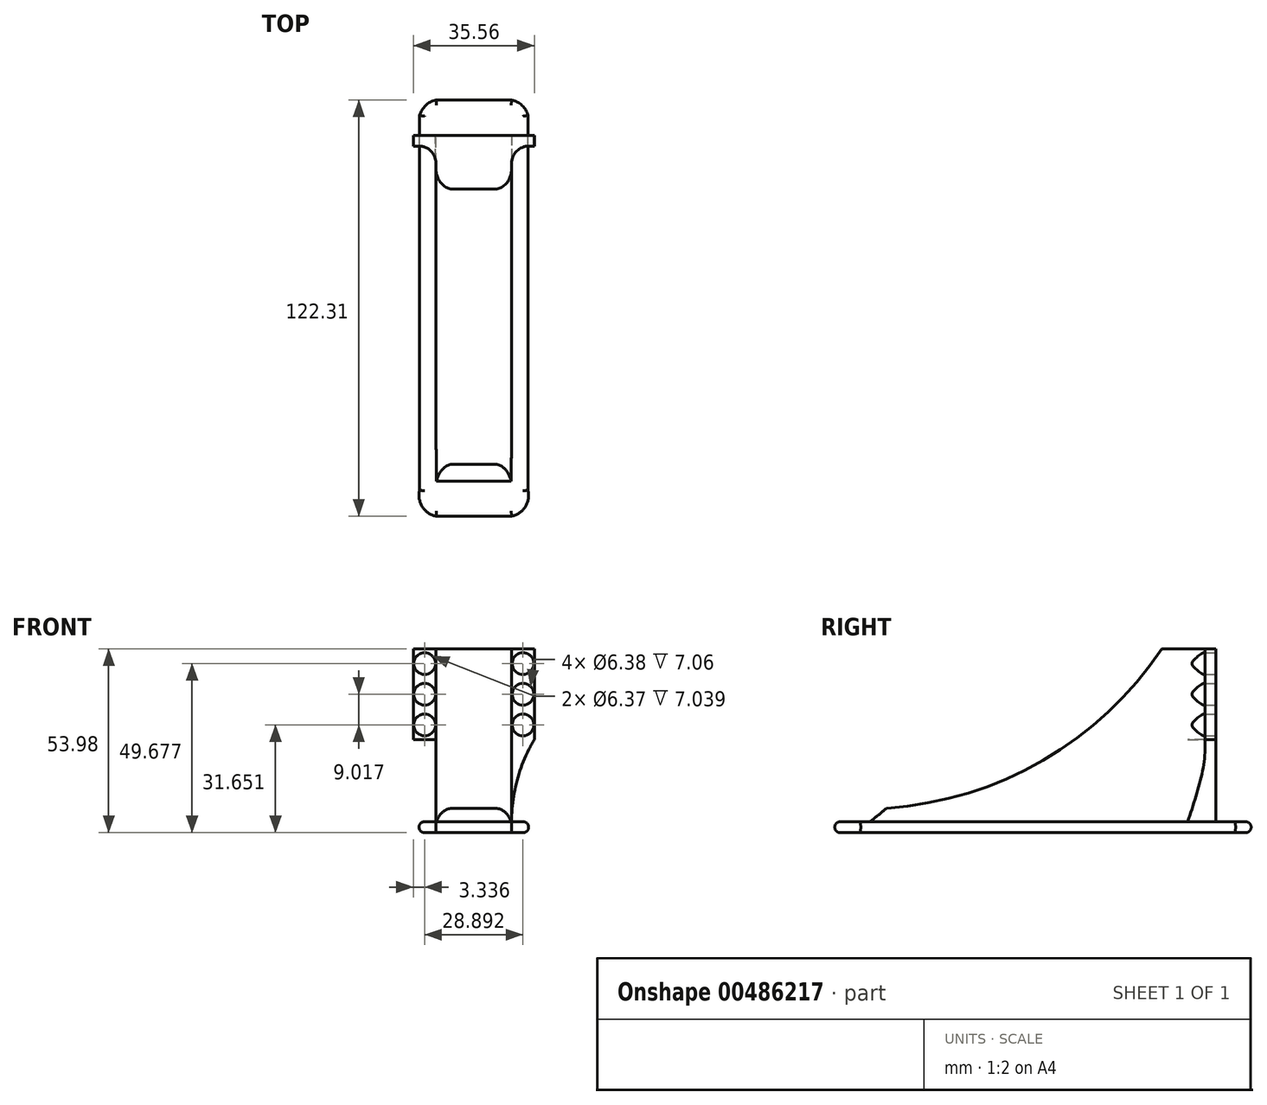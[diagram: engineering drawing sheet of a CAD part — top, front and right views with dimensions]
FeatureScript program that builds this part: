
annotation { "Feature Type Name" : "Feature", "Feature Type Description" : "" }
export const myFeature = defineFeature(function(context is Context, id is Id, definition is map)
    precondition{}
    {
        {
            var Q0;
            Q0=qCreatedBy(makeId("Right.planeOp"),FACE);
            var sketch = newSketch(context, id + "F0", { "sketchPlane" : qUnion([Q0])});
            skLineSegment(sketch, "E0", {"start": v(21.87, 0) * mm, "end": v(21.87, 50.8) * mm});
            skLineSegment(sketch, "E1", {"start": v(21.87, 0) * mm, "end": v(-54.33, 0) * mm});
            skLineSegment(sketch, "E2", {"start": v(21.87, 0) * mm, "end": v(-79.73, 0) * mm});
            skLineSegment(sketch, "E3", {"start": v(-79.73, 0) * mm, "end": v(-79.73, -3.18) * mm});
            skLineSegment(sketch, "E4", {"start": v(-79.73, -3.18) * mm, "end": v(21.87, -3.18) * mm});
            skLineSegment(sketch, "E5", {"start": v(21.87, -3.18) * mm, "end": v(21.87, 0) * mm});
            skLineSegment(sketch, "E6", {"start": v(-79.73, 0) * mm, "end": v(-74.8, 4.01) * mm});
            skLineSegment(sketch, "E7", {"start": v(21.87, 50.8) * mm, "end": v(6.02, 50.8) * mm});
            skArc(sketch, "E8", {"start": v(-74.8, 4.01) * mm, "mid": v(-28.96, 18.01) * mm, "end": v(6.02, 50.8) * mm});
            skSolve(sketch);
        }
        {
            var Q0;
            Q0=makeQuery(id+"F0.imprint","IMPRINT",FACE,{"disambiguationData":[TD([[makeQuery(id+"F0.imprint","IMPRINT",EDGE,{"derivedFrom":sQuery(id+"F0.wireOp",EDGE,"E0")}),1.0]])]});
            extrude(context, id + "F1", {"entities" : qUnion([Q0]), "depth" : 22.22 * mm, "offsetDistance" : 25.4 * mm});
        }
        {
            var Q0;
            Q0=makeQuery(id+"F1.opExtrude","SWEPT_FACE",FACE,{"disambiguationData":[OSD([sQuery(id+"F0.wireOp",EDGE,"E1"),sQuery(id+"F0.wireOp",EDGE,"E2")])]});
            var sketch = newSketch(context, id + "F2", { "sketchPlane" : qUnion([Q0])});
            skLineSegment(sketch, "E9.bottom", {"start": v(27.02, 90.08) * mm, "end": v(-4.8, 90.08) * mm});
            skLineSegment(sketch, "E9.top", {"start": v(27.02, -32.23) * mm, "end": v(-4.8, -32.23) * mm});
            skLineSegment(sketch, "E9.left", {"start": v(27.02, 90.08) * mm, "end": v(27.02, -32.23) * mm});
            skLineSegment(sketch, "E9.right", {"start": v(-4.8, 90.08) * mm, "end": v(-4.8, -32.23) * mm});
            skPoint(sketch, "E9.middle", {"position": v(11.11, 28.93) * mm});
            skPoint(sketch, "E9.middle.positionSnap0", {"position": v(22.23, 28.93) * mm});
            skPoint(sketch, "E9.middle.positionSnap1", {"position": v(11.11, 79.73) * mm});
            skPoint(sketch, "E9.centerSnap0", {"position": v(22.23, 28.93) * mm});
            skPoint(sketch, "E9.centerSnap1", {"position": v(11.11, 79.73) * mm});
            skArc(sketch, "E10", {"start": v(0, 90.08) * mm, "mid": v(-4.03, 87.29) * mm, "end": v(-4.8, 82.44) * mm});
            skLineSegment(sketch, "E11", {"start": v(11.11, 79.73) * mm, "end": v(11.11, -21.87) * mm, "construction": true});
            skLineSegment(sketch, "E12", {"start": v(11.11, 28.93) * mm, "end": v(27.02, 28.93) * mm, "construction": true});
            skArc(sketch, "E13.MirrorCS", {"start": v(22.23, 90.08) * mm, "mid": v(26.26, 87.29) * mm, "end": v(27.02, 82.44) * mm});
            skArc(sketch, "E14.MirrorCS", {"start": v(22.23, -32.23) * mm, "mid": v(26.26, -29.44) * mm, "end": v(27.02, -24.59) * mm});
            skArc(sketch, "E15.MirrorCS", {"start": v(0, -32.23) * mm, "mid": v(-4.03, -29.44) * mm, "end": v(-4.8, -24.59) * mm});
            skSolve(sketch);
        }
        {
            var Q0;
            {var subQ0=sQuery(id+"F2.wireOp",EDGE,"E13.MirrorCS");var subQ1=sQuery(id+"F2.wireOp",EDGE,"E9.left");var subQ2=makeQuery(id+"F2.imprint","INTERSECT",VERTEX,{"disambiguationData":[OD(0.0)],"derivedFrom":[subQ1,subQ0]});Q0=makeQuery(id+"F2.imprint","IMPRINT",FACE,{"disambiguationData":[TD([[makeQuery(id+"F2.imprint","IMPRINT",EDGE,{"disambiguationData":[TD([[subQ2,1.0]])],"derivedFrom":subQ1}),1.0]])]});}
            var Q1;
            {var subQ0=sQuery(id+"F2.wireOp",EDGE,"E14.MirrorCS");var subQ1=sQuery(id+"F2.wireOp",EDGE,"E9.left");var subQ2=makeQuery(id+"F2.imprint","INTERSECT",VERTEX,{"disambiguationData":[OD(0.0)],"derivedFrom":[subQ1,subQ0]});Q1=makeQuery(id+"F2.imprint","IMPRINT",FACE,{"disambiguationData":[TD([[makeQuery(id+"F2.imprint","IMPRINT",EDGE,{"disambiguationData":[TD([[subQ2,-1.0]])],"derivedFrom":subQ1}),1.0]])]});}
            var Q2;
            {var subQ0=sQuery(id+"F2.wireOp",EDGE,"E10");var subQ1=sQuery(id+"F2.wireOp",EDGE,"E9.right");var subQ2=makeQuery(id+"F2.imprint","INTERSECT",VERTEX,{"disambiguationData":[OD(0.0)],"derivedFrom":[subQ1,subQ0]});Q2=makeQuery(id+"F2.imprint","IMPRINT",FACE,{"disambiguationData":[TD([[makeQuery(id+"F2.imprint","IMPRINT",EDGE,{"disambiguationData":[TD([[subQ2,1.0]])],"derivedFrom":subQ1}),-1.0]])]});}
            var Q3;
            {var subQ0=sQuery(id+"F2.wireOp",EDGE,"E15.MirrorCS");var subQ1=sQuery(id+"F2.wireOp",EDGE,"E9.right");var subQ2=makeQuery(id+"F2.imprint","INTERSECT",VERTEX,{"disambiguationData":[OD(0.0)],"derivedFrom":[subQ1,subQ0]});Q3=makeQuery(id+"F2.imprint","IMPRINT",FACE,{"disambiguationData":[TD([[makeQuery(id+"F2.imprint","IMPRINT",EDGE,{"disambiguationData":[TD([[subQ2,-1.0]])],"derivedFrom":subQ1}),-1.0]])]});}
            var Q4;
            {var subQ0=sQuery(id+"F0.wireOp",EDGE,"E1");var subQ1=sQuery(id+"F0.wireOp",EDGE,"E2");Q4=makeQuery(id+"F2.imprint","IMPRINT",FACE,{"disambiguationData":[TD([[makeQuery(id+"F2.imprint","IMPRINT",EDGE,{"derivedFrom":makeQuery(id+"F1.opExtrude","CAP_EDGE",EDGE,{"disambiguationData":[OSD([subQ0,subQ1])],"isStart":true})}),-1.0]])]});}
            var Q5;
            {var subQ15=sQuery(id+"F0.wireOp",EDGE,"E1");var subQ19=sQuery(id+"F0.wireOp",EDGE,"E2");Q5=makeQuery(id+"F2.imprint","IMPRINT",FACE,{"disambiguationData":[TD([[makeQuery(id+"F2.imprint","IMPRINT",EDGE,{"derivedFrom":makeQuery(id+"F1.opExtrude","CAP_EDGE",EDGE,{"disambiguationData":[OSD([subQ15,subQ19])],"isStart":true})}),1.0]])]});}
            extrude(context, id + "F3", {"entities" : qUnion([Q0, Q1, Q2, Q3, Q4, Q5]), "operationType" : NewBodyOperationType.ADD, "depth" : 3.17 * mm, "offsetDistance" : 25.4 * mm});
        }
        {
            var Q0;
            Q0=makeQuery(id+"F1.opExtrude","SWEPT_FACE",FACE,{"disambiguationData":[OSD([sQuery(id+"F0.wireOp",EDGE,"E0")])]});
            var sketch = newSketch(context, id + "F4", { "sketchPlane" : qUnion([Q0])});
            skLineSegment(sketch, "E16.bottom", {"start": v(-11.11, 50.8) * mm, "end": v(6.67, 50.8) * mm});
            skLineSegment(sketch, "E16.top", {"start": v(-11.11, 24.18) * mm, "end": v(6.67, 24.18) * mm});
            skLineSegment(sketch, "E16.left", {"start": v(-11.11, 50.8) * mm, "end": v(-11.11, 24.18) * mm});
            skLineSegment(sketch, "E16.right", {"start": v(6.67, 50.8) * mm, "end": v(6.67, 24.18) * mm});
            skLineSegment(sketch, "E17", {"start": v(0, 50.8) * mm, "end": v(6.67, 50.8) * mm, "construction": true});
            skLineSegment(sketch, "E18", {"start": v(3.33, 50.8) * mm, "end": v(3.33, 24.18) * mm, "construction": true});
            skCircle(sketch, "E19", {"center": v(3.33, 46.5) * mm, "radius": 3.18 * mm});
            skLineSegment(sketch, "E20", {"start": v(3.33, 43.31) * mm, "end": v(3.33, 39.35) * mm, "construction": true});
            skCircle(sketch, "E21", {"center": v(3.33, 37.49) * mm, "radius": 3.19 * mm});
            skLineSegment(sketch, "E22", {"start": v(3.33, 46.5) * mm, "end": v(3.33, 37.49) * mm});
            skLineSegment(sketch, "E23", {"start": v(3.33, 37.49) * mm, "end": v(3.33, 28.47) * mm});
            skCircle(sketch, "E24", {"center": v(3.33, 28.47) * mm, "radius": 3.19 * mm});
            skLineSegment(sketch, "E25.MirrorCS", {"start": v(-11.11, 50.8) * mm, "end": v(-28.9, 50.8) * mm});
            skLineSegment(sketch, "E26.MirrorCS", {"start": v(-11.11, 24.18) * mm, "end": v(-28.9, 24.18) * mm});
            skLineSegment(sketch, "E27.MirrorCS", {"start": v(-28.9, 50.8) * mm, "end": v(-28.9, 24.18) * mm});
            skCircle(sketch, "E28.MirrorC", {"center": v(-25.56, 37.49) * mm, "radius": 3.19 * mm});
            skCircle(sketch, "E29.MirrorC", {"center": v(-25.56, 28.47) * mm, "radius": 3.19 * mm});
            skCircle(sketch, "E30.MirrorC", {"center": v(-25.56, 46.5) * mm, "radius": 3.18 * mm});
            skArc(sketch, "E31", {"start": v(-22.22, 0) * mm, "mid": v(-23.92, 12.54) * mm, "end": v(-28.9, 24.18) * mm});
            skArc(sketch, "E32.MirrorCS", {"start": v(0, 0) * mm, "mid": v(1.7, 12.54) * mm, "end": v(6.67, 24.18) * mm});
            skSolve(sketch);
        }
        {
            var Q0;
            Q0 = qSketchRegion(id + "F4", true);
            var Q1;
            {var subQ0=sQuery(id+"F4.wireOp",EDGE,"E32.MirrorCS");Q1=makeQuery(id+"F4.imprint","IMPRINT",FACE,{"disambiguationData":[TD([[makeQuery(id+"F4.imprint","IMPRINT",EDGE,{"derivedFrom":subQ0}),1.0]])]});}
            var Q2;
            {var subQ0=sQuery(id+"F4.wireOp",EDGE,"E31");Q2=makeQuery(id+"F4.imprint","IMPRINT",FACE,{"disambiguationData":[TD([[makeQuery(id+"F4.imprint","IMPRINT",EDGE,{"derivedFrom":subQ0}),-1.0]])]});}
            extrude(context, id + "F5", {"entities" : qUnion([Q0, Q1, Q2]), "operationType" : NewBodyOperationType.ADD, "oppositeDirection" : true, "depth" : 3.17 * mm, "offsetDistance" : 25.4 * mm});
        }
        {
            var Q0;
            Q0=makeQuery(id+"F1.opExtrude","CAP_EDGE",EDGE,{"disambiguationData":[OSD([sQuery(id+"F0.wireOp",EDGE,"E8")])],"isStart":false});
            var Q1;
            Q1=makeQuery(id+"F1.opExtrude","CAP_EDGE",EDGE,{"disambiguationData":[OSD([sQuery(id+"F0.wireOp",EDGE,"E8")])],"isStart":true});
            var Q2;
            {var subQ0=sQuery(id+"F0.wireOp",EDGE,"E0");Q2=makeQuery(id+"F5.boolean.opBoolean","INTERSECT",EDGE,{"derivedFrom":[makeQuery(id+"F1.opExtrude","CAP_FACE",FACE,{"disambiguationData":[OSD([subQ0,sQuery(id+"F0.wireOp",EDGE,"E1"),sQuery(id+"F0.wireOp",EDGE,"E2"),sQuery(id+"F0.wireOp",EDGE,"E6"),sQuery(id+"F0.wireOp",EDGE,"E7"),sQuery(id+"F0.wireOp",EDGE,"E8")])],"isStart":false}),makeQuery(id+"F5.opExtrude","CAP_FACE",FACE,{"disambiguationData":[OSD([subQ0,sQuery(id+"F4.wireOp",EDGE,"E16.bottom"),sQuery(id+"F4.wireOp",EDGE,"E16.top"),sQuery(id+"F4.wireOp",EDGE,"E16.right"),sQuery(id+"F4.wireOp",EDGE,"E19"),sQuery(id+"F4.wireOp",EDGE,"E21"),sQuery(id+"F4.wireOp",EDGE,"E24"),sQuery(id+"F4.wireOp",EDGE,"E25.MirrorCS"),sQuery(id+"F4.wireOp",EDGE,"E26.MirrorCS"),sQuery(id+"F4.wireOp",EDGE,"E27.MirrorCS"),sQuery(id+"F4.wireOp",EDGE,"E28.MirrorC"),sQuery(id+"F4.wireOp",EDGE,"E29.MirrorC"),sQuery(id+"F4.wireOp",EDGE,"E30.MirrorC"),sQuery(id+"F4.wireOp",EDGE,"E31"),sQuery(id+"F4.wireOp",EDGE,"E32.MirrorCS")])],"isStart":false})]});}
            var Q3;
            {var subQ0=sQuery(id+"F0.wireOp",EDGE,"E0");Q3=makeQuery(id+"F5.boolean.opBoolean","INTERSECT",EDGE,{"derivedFrom":[makeQuery(id+"F1.opExtrude","CAP_FACE",FACE,{"disambiguationData":[OSD([subQ0,sQuery(id+"F0.wireOp",EDGE,"E1"),sQuery(id+"F0.wireOp",EDGE,"E2"),sQuery(id+"F0.wireOp",EDGE,"E6"),sQuery(id+"F0.wireOp",EDGE,"E7"),sQuery(id+"F0.wireOp",EDGE,"E8")])],"isStart":true}),makeQuery(id+"F5.opExtrude","CAP_FACE",FACE,{"disambiguationData":[OSD([subQ0,sQuery(id+"F4.wireOp",EDGE,"E16.bottom"),sQuery(id+"F4.wireOp",EDGE,"E16.top"),sQuery(id+"F4.wireOp",EDGE,"E16.right"),sQuery(id+"F4.wireOp",EDGE,"E19"),sQuery(id+"F4.wireOp",EDGE,"E21"),sQuery(id+"F4.wireOp",EDGE,"E24"),sQuery(id+"F4.wireOp",EDGE,"E25.MirrorCS"),sQuery(id+"F4.wireOp",EDGE,"E26.MirrorCS"),sQuery(id+"F4.wireOp",EDGE,"E27.MirrorCS"),sQuery(id+"F4.wireOp",EDGE,"E28.MirrorC"),sQuery(id+"F4.wireOp",EDGE,"E29.MirrorC"),sQuery(id+"F4.wireOp",EDGE,"E30.MirrorC"),sQuery(id+"F4.wireOp",EDGE,"E31"),sQuery(id+"F4.wireOp",EDGE,"E32.MirrorCS")])],"isStart":false})]});}
            fillet(context, id + "F6", {"entities" : qUnion([Q0, Q1, Q2, Q3]), "radius" : 5.08 * mm, "tangentPropagation" : true, "allowEdgeOverflow" : false});
        }
        {
            var Q0;
            Q0=makeQuery(id+"F3.opExtrude","CAP_EDGE",EDGE,{"disambiguationData":[OSD([sQuery(id+"F2.wireOp",EDGE,"E9.left")])],"isStart":true});
            var Q1;
            Q1=makeQuery(id+"F3.opExtrude","CAP_EDGE",EDGE,{"disambiguationData":[OSD([sQuery(id+"F2.wireOp",EDGE,"E13.MirrorCS")])],"isStart":true});
            var Q2;
            Q2=makeQuery(id+"F3.opExtrude","CAP_EDGE",EDGE,{"disambiguationData":[OSD([sQuery(id+"F2.wireOp",EDGE,"E9.bottom")])],"isStart":true});
            var Q3;
            Q3=makeQuery(id+"F3.opExtrude","CAP_EDGE",EDGE,{"disambiguationData":[OSD([sQuery(id+"F2.wireOp",EDGE,"E10")])],"isStart":true});
            var Q4;
            Q4=makeQuery(id+"F3.opExtrude","CAP_EDGE",EDGE,{"disambiguationData":[OSD([sQuery(id+"F2.wireOp",EDGE,"E9.right")])],"isStart":true});
            var Q5;
            Q5=makeQuery(id+"F3.opExtrude","CAP_EDGE",EDGE,{"disambiguationData":[OSD([sQuery(id+"F2.wireOp",EDGE,"E14.MirrorCS")])],"isStart":true});
            var Q6;
            Q6=makeQuery(id+"F3.opExtrude","CAP_EDGE",EDGE,{"disambiguationData":[OSD([sQuery(id+"F2.wireOp",EDGE,"E15.MirrorCS")])],"isStart":true});
            var Q7;
            Q7=makeQuery(id+"F3.opExtrude","CAP_EDGE",EDGE,{"disambiguationData":[OSD([sQuery(id+"F2.wireOp",EDGE,"E14.MirrorCS")])],"isStart":false});
            var Q8;
            Q8=makeQuery(id+"F3.opExtrude","CAP_EDGE",EDGE,{"disambiguationData":[OSD([sQuery(id+"F2.wireOp",EDGE,"E9.top")])],"isStart":false});
            var Q9;
            Q9=makeQuery(id+"F3.opExtrude","CAP_EDGE",EDGE,{"disambiguationData":[OSD([sQuery(id+"F2.wireOp",EDGE,"E15.MirrorCS")])],"isStart":false});
            var Q10;
            Q10=makeQuery(id+"F3.opExtrude","CAP_EDGE",EDGE,{"disambiguationData":[OSD([sQuery(id+"F2.wireOp",EDGE,"E9.left")])],"isStart":false});
            var Q11;
            Q11=makeQuery(id+"F3.opExtrude","CAP_EDGE",EDGE,{"disambiguationData":[OSD([sQuery(id+"F2.wireOp",EDGE,"E9.right")])],"isStart":false});
            var Q12;
            Q12=makeQuery(id+"F3.opExtrude","CAP_EDGE",EDGE,{"disambiguationData":[OSD([sQuery(id+"F2.wireOp",EDGE,"E10")])],"isStart":false});
            var Q13;
            Q13=makeQuery(id+"F3.opExtrude","CAP_EDGE",EDGE,{"disambiguationData":[OSD([sQuery(id+"F2.wireOp",EDGE,"E9.bottom")])],"isStart":false});
            var Q14;
            Q14=makeQuery(id+"F3.opExtrude","CAP_EDGE",EDGE,{"disambiguationData":[OSD([sQuery(id+"F2.wireOp",EDGE,"E13.MirrorCS")])],"isStart":false});
            var Q15;
            Q15=makeQuery(id+"F3.opExtrude","CAP_EDGE",EDGE,{"disambiguationData":[OSD([sQuery(id+"F2.wireOp",EDGE,"E9.top")])],"isStart":true});
            fillet(context, id + "F7", {"entities" : qUnion([Q0, Q1, Q2, Q3, Q4, Q5, Q6, Q7, Q8, Q9, Q10, Q11, Q12, Q13, Q14, Q15]), "radius" : 1.52 * mm, "tangentPropagation" : true, "allowEdgeOverflow" : false});
        }
    });
